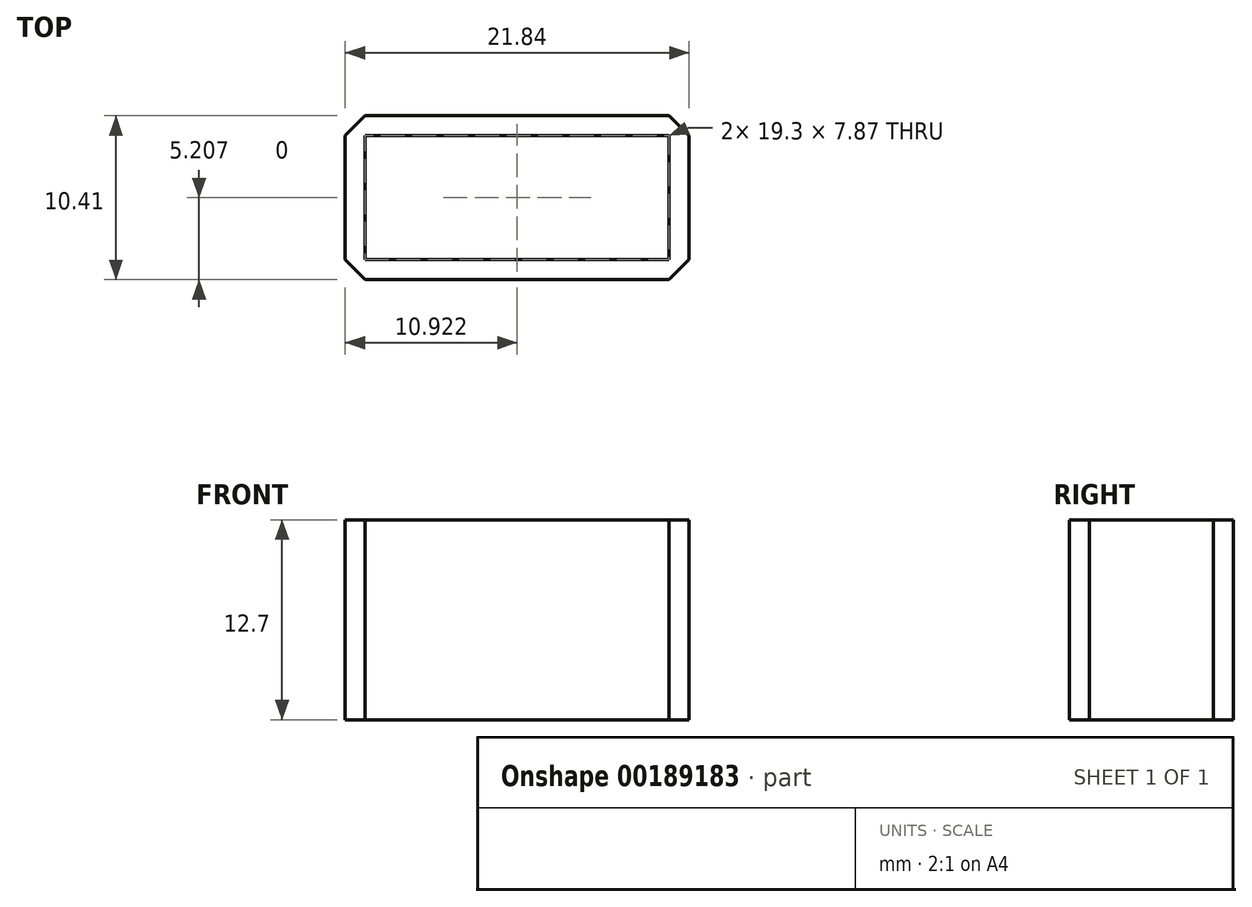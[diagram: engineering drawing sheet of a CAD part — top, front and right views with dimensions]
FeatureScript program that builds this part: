
annotation { "Feature Type Name" : "Feature", "Feature Type Description" : "" }
export const myFeature = defineFeature(function(context is Context, id is Id, definition is map)
    precondition{}
    {
        {
            var Q0;
            Q0=qCreatedBy(makeId("Top.planeOp"),FACE);
            var sketch = newSketch(context, id + "F0", { "sketchPlane" : qUnion([Q0])});
            skLineSegment(sketch, "E0.bottom", {"start": v(0, 0) * mm, "end": v(19.3, 0) * mm});
            skLineSegment(sketch, "E0.top", {"start": v(0, 7.87) * mm, "end": v(19.3, 7.87) * mm});
            skLineSegment(sketch, "E0.left", {"start": v(0, 0) * mm, "end": v(0, 7.87) * mm});
            skLineSegment(sketch, "E0.right", {"start": v(19.3, 0) * mm, "end": v(19.3, 7.87) * mm});
            skLineSegment(sketch, "E1", {"start": v(6.77, 7.87) * mm, "end": v(6.77, 9.14) * mm});
            skLineSegment(sketch, "E2", {"start": v(0, 7.87) * mm, "end": v(0, 9.14) * mm});
            skLineSegment(sketch, "E3", {"start": v(0, 9.14) * mm, "end": v(6.77, 9.14) * mm});
            skLineSegment(sketch, "E4", {"start": v(19.3, 7.87) * mm, "end": v(19.3, 9.14) * mm});
            skLineSegment(sketch, "E5", {"start": v(19.3, 9.14) * mm, "end": v(6.77, 9.14) * mm});
            skLineSegment(sketch, "E6", {"start": v(19.3, 7.87) * mm, "end": v(20.57, 7.87) * mm});
            skLineSegment(sketch, "E7", {"start": v(19.3, 9.14) * mm, "end": v(20.57, 7.87) * mm});
            skLineSegment(sketch, "E8", {"start": v(19.3, 0) * mm, "end": v(20.57, 0) * mm});
            skLineSegment(sketch, "E9", {"start": v(20.57, 0) * mm, "end": v(20.57, 7.87) * mm});
            skLineSegment(sketch, "E10", {"start": v(19.3, 0) * mm, "end": v(19.3, -1.27) * mm});
            skLineSegment(sketch, "E11", {"start": v(19.3, -1.27) * mm, "end": v(20.57, 0) * mm});
            skLineSegment(sketch, "E12", {"start": v(0, 0) * mm, "end": v(0, -1.27) * mm});
            skLineSegment(sketch, "E13", {"start": v(0, -1.27) * mm, "end": v(19.3, -1.27) * mm});
            skLineSegment(sketch, "E14", {"start": v(0, 0) * mm, "end": v(-1.27, 0) * mm});
            skLineSegment(sketch, "E15", {"start": v(0, -1.27) * mm, "end": v(-1.27, 0) * mm});
            skLineSegment(sketch, "E16", {"start": v(0, 7.87) * mm, "end": v(-1.27, 7.87) * mm});
            skLineSegment(sketch, "E17", {"start": v(-1.27, 7.87) * mm, "end": v(-1.27, 0) * mm});
            skLineSegment(sketch, "E18", {"start": v(-1.27, 7.87) * mm, "end": v(0, 9.14) * mm});
            skSolve(sketch);
        }
        {
            var Q0;
            Q0=makeQuery(id+"F0.imprint","IMPRINT",FACE,{"disambiguationData":[TD([[makeQuery(id+"F0.imprint","IMPRINT",EDGE,{"derivedFrom":sQuery(id+"F0.wireOp",EDGE,"E0.bottom")}),-1.0]])]});
            var Q1;
            Q1=makeQuery(id+"F0.imprint","IMPRINT",FACE,{"disambiguationData":[TD([[makeQuery(id+"F0.imprint","IMPRINT",EDGE,{"derivedFrom":sQuery(id+"F0.wireOp",EDGE,"E8")}),-1.0]])]});
            var Q2;
            Q2=makeQuery(id+"F0.imprint","IMPRINT",FACE,{"disambiguationData":[TD([[makeQuery(id+"F0.imprint","IMPRINT",EDGE,{"derivedFrom":sQuery(id+"F0.wireOp",EDGE,"E0.right")}),-1.0]])]});
            var Q3;
            Q3=makeQuery(id+"F0.imprint","IMPRINT",FACE,{"disambiguationData":[TD([[makeQuery(id+"F0.imprint","IMPRINT",EDGE,{"derivedFrom":sQuery(id+"F0.wireOp",EDGE,"E4")}),-1.0]])]});
            var Q4;
            {var subQ2=sQuery(id+"F0.wireOp",EDGE,"E1");Q4=makeQuery(id+"F0.imprint","IMPRINT",FACE,{"disambiguationData":[TD([[makeQuery(id+"F0.imprint","IMPRINT",EDGE,{"derivedFrom":subQ2}),-1.0]])]});}
            var Q5;
            {var subQ2=sQuery(id+"F0.wireOp",EDGE,"E1");Q5=makeQuery(id+"F0.imprint","IMPRINT",FACE,{"disambiguationData":[TD([[makeQuery(id+"F0.imprint","IMPRINT",EDGE,{"derivedFrom":subQ2}),1.0]])]});}
            var Q6;
            Q6=makeQuery(id+"F0.imprint","IMPRINT",FACE,{"disambiguationData":[TD([[makeQuery(id+"F0.imprint","IMPRINT",EDGE,{"derivedFrom":sQuery(id+"F0.wireOp",EDGE,"E2")}),1.0]])]});
            var Q7;
            Q7=makeQuery(id+"F0.imprint","IMPRINT",FACE,{"disambiguationData":[TD([[makeQuery(id+"F0.imprint","IMPRINT",EDGE,{"derivedFrom":sQuery(id+"F0.wireOp",EDGE,"E0.left")}),1.0]])]});
            var Q8;
            Q8=makeQuery(id+"F0.imprint","IMPRINT",FACE,{"disambiguationData":[TD([[makeQuery(id+"F0.imprint","IMPRINT",EDGE,{"derivedFrom":sQuery(id+"F0.wireOp",EDGE,"E12")}),-1.0]])]});
            extrude(context, id + "F1", {"entities" : qUnion([Q0, Q1, Q2, Q3, Q4, Q5, Q6, Q7, Q8]), "depth" : 12.7 * mm});
        }
        {
            var Q0;
            Q0 = qSketchRegion(id + "F0", true);
            extrude(context, id + "F2", {"entities" : qUnion([Q0]), "depth" : 12.7 * mm});
        }
    });
